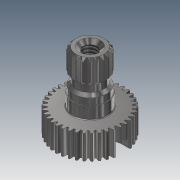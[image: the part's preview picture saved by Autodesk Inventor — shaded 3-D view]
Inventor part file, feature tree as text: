
AUTODESK INVENTOR PART (.ipt)
format: ipt  version: 2017 (Build 210142000, 142)  size: 541,184 bytes
history: native  units: mm (DEFAULTED — no unit token found)
features: sketch x7, extrude x4, plane x3, other x3, chamfer x3, revolve x1, fillet x1, hole x1, pattern_circular x1
ambient origin geometry x8: Origin, YZ Plane, XZ Plane, XY Plane, X Axis, Y Axis, Z Axis, Center Point
bodies: Solid1 (feature_tree)
feature tree (24):
  extrude  "Extrusion1"  Depth=10.0mm TaperAngle=0.0deg
  plane  "Work Plane2"
  plane  "Work Plane8"
  plane  "Work Plane9"
  other  "Цилиндрическое зубчатое зацепление"
  revolve  "Вращение1"
  fillet  "Сопряжение1"  Radius=9.5mm
  chamfer  "Фаска1"  Distance=10.0mm
  hole  "Отверстие1"  [1 undecoded]
  chamfer  "Фаска2"  [1 undecoded]
  extrude  "Выдавливание2"  TaperAngle=0.0deg  [1 undecoded]
  extrude  "Выдавливание3"  Depth=6.0mm
  extrude  "Выдавливание4"  Depth=6.0mm
  pattern_circular  "Круговой массив1"  [2 undecoded]
  chamfer  "Фаска3"  Distance=7.5mm
  sketch  "Sketch1"  dims[d0=9.865mm d1=3.5mm d2=0.0mm d3=9.5mm d4=10.0mm d5=0.0mm]
  sketch  "Sketch2"  dims[d16=6.0mm d17=0.0mm d34=0.826735mm d39=0.0mm d41=0.0mm d43=6.0mm d46=6.0mm d47=0.0mm d48=0.0mm d49=7.5mm d50=4.8mm d51=4.0mm d52=4.8mm d53=5.0mm d55=1.75mm d56=1.0mm d57=4.1mm d58=3.4mm d59=90.0deg d60=0.1mm d61=0.4mm d62=2.0mm d63=45.0deg d64=2.013mm d65=11.0mm d66=3.4mm d67=4.5mm d68=14.3117mm d69=11.0mm d70=20.594885mm d71=0.2mm d72=2.0mm d73=45.0deg d74=7.0mm d75=1.0mm d76=0.0mm d77=6.0mm d78=2.0mm d79=1.5mm d80=0.0mm d82=3.141593mm d86=0.05mm d87=0.05mm d88=0.1mm d89=3.5mm d90=0.0mm d91=200.0mm d92=360.0deg d94=0.5mm d95=2.0mm d96=45.0deg]
  other  "Srf1"
  sketch  "Эскиз3"
  sketch  "Эскиз4"
  sketch  "Эскиз5"
  sketch  "Эскиз6"
  sketch  "Эскиз7"
  other  "Средний диаметр"
note: 5 required parameter values undecoded (feature->parameter linkage not recoverable at this tier; creation-order binding heuristic only, values carry confidence <= 0.55)
